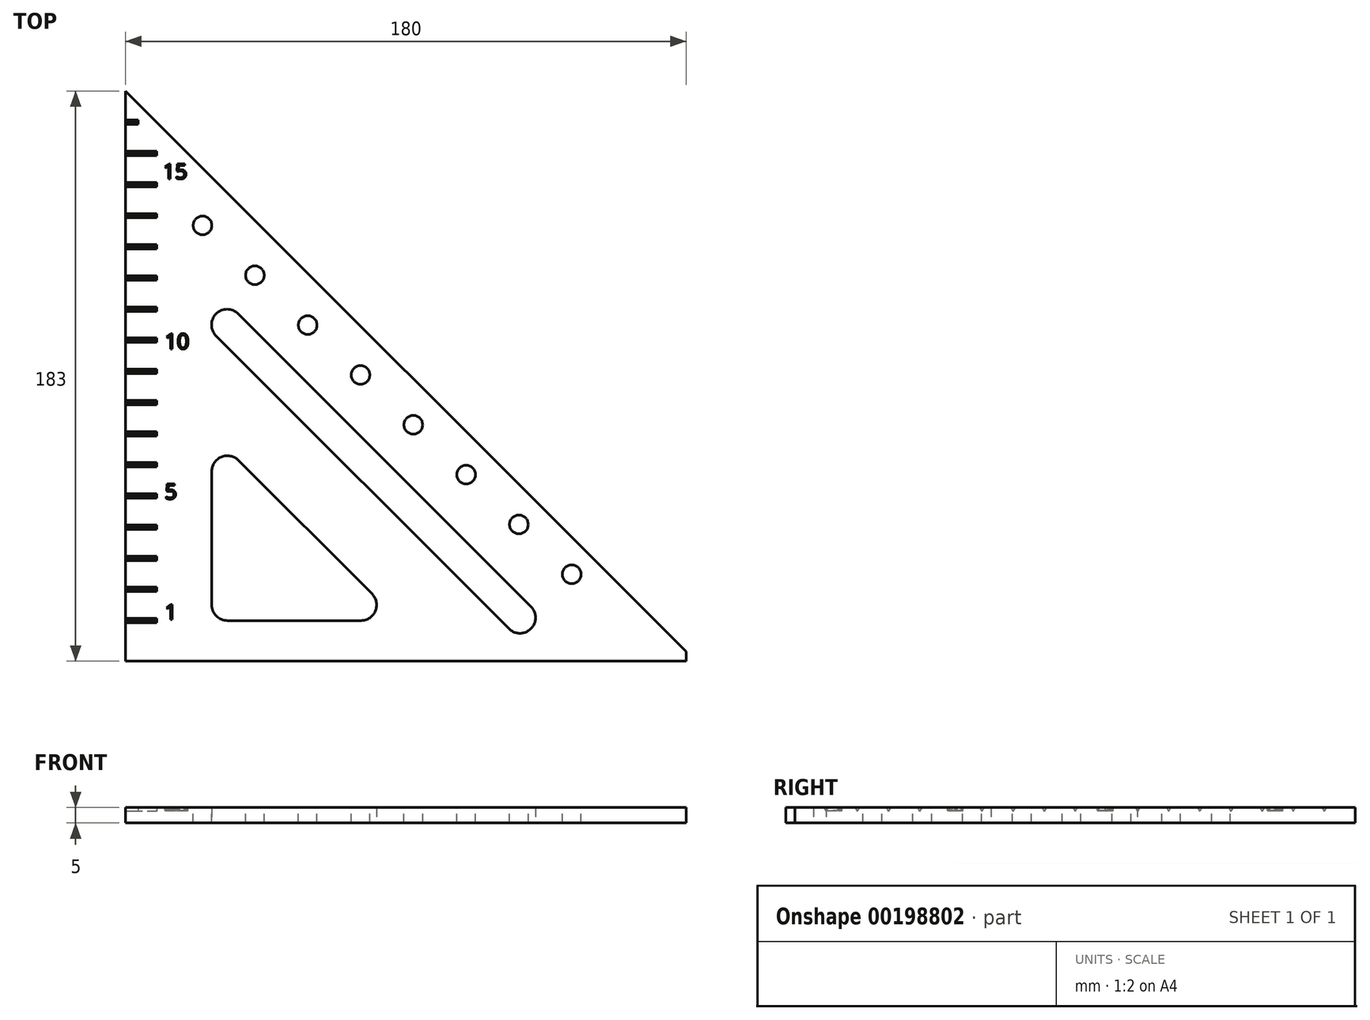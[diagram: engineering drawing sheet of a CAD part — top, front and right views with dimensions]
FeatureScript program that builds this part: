
annotation { "Feature Type Name" : "Feature", "Feature Type Description" : "" }
export const myFeature = defineFeature(function(context is Context, id is Id, definition is map)
    precondition{}
    {
        {
            var Q0;
            Q0=qCreatedBy(makeId("Top.planeOp"),FACE);
            var sketch = newSketch(context, id + "F0", { "sketchPlane" : qUnion([Q0])});
            skLineSegment(sketch, "E0", {"start": v(-55.4, -72.48) * mm, "end": v(124.6, -72.48) * mm});
            skLineSegment(sketch, "E1", {"start": v(124.6, -72.48) * mm, "end": v(-55.4, 107.52) * mm});
            skLineSegment(sketch, "E2", {"start": v(-55.4, 107.52) * mm, "end": v(-55.4, -72.48) * mm});
            skLineSegment(sketch, "E3", {"start": v(-73.6, 83.28) * mm, "end": v(83.51, -73.83) * mm, "construction": true});
            skLineSegment(sketch, "E4", {"start": v(-27.73, -14.56) * mm, "end": v(-27.73, -57.48) * mm});
            skLineSegment(sketch, "E5", {"start": v(-22.73, -62.48) * mm, "end": v(20.2, -62.48) * mm});
            skLineSegment(sketch, "E6", {"start": v(23.74, -53.95) * mm, "end": v(-19.19, -11.02) * mm});
            skPoint(sketch, "E7.visualSharp", {"position": v(-27.73, -62.48) * mm});
            skArc(sketch, "E7.filletArc", {"start": v(-27.73, -57.48) * mm, "mid": v(-26.26, -61.02) * mm, "end": v(-22.73, -62.48) * mm});
            skPoint(sketch, "E8.visualSharp", {"position": v(32.27, -62.48) * mm});
            skArc(sketch, "E8.filletArc", {"start": v(20.2, -62.48) * mm, "mid": v(24.82, -59.4) * mm, "end": v(23.74, -53.95) * mm});
            skPoint(sketch, "E9.visualSharp", {"position": v(-27.73, -2.48) * mm});
            skArc(sketch, "E9.filletArc", {"start": v(-19.19, -11.02) * mm, "mid": v(-24.64, -9.94) * mm, "end": v(-27.73, -14.56) * mm});
            skLineSegment(sketch, "E10", {"start": v(-19.27, 36.02) * mm, "end": v(74.78, -58.03) * mm});
            skLineSegment(sketch, "E11.MirrorCS", {"start": v(-26.34, 28.95) * mm, "end": v(67.7, -65.1) * mm});
            skLineSegment(sketch, "E12", {"start": v(-27.73, -25.02) * mm, "end": v(-27.73, 82.1) * mm, "construction": true});
            skArc(sketch, "E13", {"start": v(-19.27, 36.02) * mm, "mid": v(-26.34, 36.02) * mm, "end": v(-26.34, 28.95) * mm});
            skArc(sketch, "E14", {"start": v(67.7, -65.1) * mm, "mid": v(74.78, -65.1) * mm, "end": v(74.78, -58.03) * mm});
            skLineSegment(sketch, "E15", {"start": v(-55.4, -98.03) * mm, "end": v(-55.4, 125.94) * mm, "construction": true});
            skLineSegment(sketch, "E16", {"start": v(-63.27, -62.48) * mm, "end": v(-48.03, -62.48) * mm, "construction": true});
            skLineSegment(sketch, "E17.bottom", {"start": v(-55.4, -72.48) * mm, "end": v(124.59, -72.48) * mm});
            skLineSegment(sketch, "E17.top", {"start": v(-55.4, -75.48) * mm, "end": v(124.59, -75.48) * mm});
            skLineSegment(sketch, "E17.left", {"start": v(-55.4, -72.48) * mm, "end": v(-55.4, -75.48) * mm});
            skLineSegment(sketch, "E17.right", {"start": v(124.59, -72.48) * mm, "end": v(124.59, -75.48) * mm});
            skLineSegment(sketch, "E18", {"start": v(-62.17, 97.41) * mm, "end": v(117.66, -82.41) * mm, "construction": true});
            skLineSegment(sketch, "E19", {"start": v(-55.4, -72.48) * mm, "end": v(144.22, -19) * mm, "construction": true});
            skLineSegment(sketch, "E20", {"start": v(-55.4, -72.48) * mm, "end": v(114.68, 25.72) * mm, "construction": true});
            skLineSegment(sketch, "E21", {"start": v(-55.4, -72.48) * mm, "end": v(71.5, 54.43) * mm, "construction": true});
            skLineSegment(sketch, "E22", {"start": v(-55.4, -72.48) * mm, "end": v(37.85, 89.04) * mm, "construction": true});
            skLineSegment(sketch, "E23", {"start": v(-55.4, -72.48) * mm, "end": v(-6.43, 110.3) * mm, "construction": true});
            skLineSegment(sketch, "E24", {"start": v(73.26, -38) * mm, "end": v(86.55, -34.45) * mm});
            skLineSegment(sketch, "E25", {"start": v(48.02, -12.77) * mm, "end": v(58.7, -6.6) * mm});
            skLineSegment(sketch, "E26", {"start": v(26.16, 9.09) * mm, "end": v(34.6, 17.52) * mm});
            skLineSegment(sketch, "E27", {"start": v(4.3, 30.94) * mm, "end": v(10.47, 41.63) * mm});
            skLineSegment(sketch, "E28", {"start": v(-20.93, 56.18) * mm, "end": v(-17.37, 69.48) * mm});
            skSolve(sketch);
        }
        {
            var Q0;
            Q0 = qSketchRegion(id + "F0", true);
            extrude(context, id + "F1", {"entities" : qUnion([Q0]), "endBound" : BoundingType.SYMMETRIC, "depth" : 5 * mm});
        }
        {
            var Q0;
            Q0=makeQuery(id+"F1.opExtrude","SWEPT_FACE",FACE,{"disambiguationData":[OSD([sQuery(id+"F0.wireOp",EDGE,"E2"),sQuery(id+"F0.wireOp",EDGE,"E17.left")])]});
            cPlane(context, id + "F2", {"entities" : qUnion([Q0]), "cplaneType" : CPlaneType.OFFSET, "offset" : 0 * mm, "width" : 150 * mm, "height" : 150 * mm});
        }
        {
            var Q0;
            Q0=qCreatedBy(id+"F2.planeOp",FACE);
            var sketch = newSketch(context, id + "F3", { "sketchPlane" : qUnion([Q0])});
            skLineSegment(sketch, "E29", {"start": v(72.48, 5.08) * mm, "end": v(72.48, -6.06) * mm, "construction": true});
            skLineSegment(sketch, "E30", {"start": v(62.48, 3.35) * mm, "end": v(62.48, -6.25) * mm, "construction": true});
            skLineSegment(sketch, "E31", {"start": v(62.48, 2.51) * mm, "end": v(61.78, 2.51) * mm});
            skLineSegment(sketch, "E32", {"start": v(61.78, 2.51) * mm, "end": v(62.48, 1.19) * mm});
            skLineSegment(sketch, "E33.MirrorCS", {"start": v(62.48, -0.72) * mm, "end": v(62.48, 8.88) * mm, "construction": true});
            skLineSegment(sketch, "E34.MirrorCS", {"start": v(62.48, 2.51) * mm, "end": v(63.18, 2.51) * mm});
            skLineSegment(sketch, "E35.MirrorCS", {"start": v(63.18, 2.51) * mm, "end": v(62.48, 1.19) * mm});
            skLineSegment(sketch, "E36.1.0.0", {"start": v(51.78, 2.51) * mm, "end": v(52.48, 1.19) * mm});
            skLineSegment(sketch, "E36.1.0.1", {"start": v(53.18, 2.51) * mm, "end": v(52.48, 1.19) * mm});
            skLineSegment(sketch, "E36.1.0.2", {"start": v(52.48, 2.51) * mm, "end": v(51.78, 2.51) * mm});
            skLineSegment(sketch, "E36.1.0.3", {"start": v(52.48, 2.51) * mm, "end": v(53.18, 2.51) * mm});
            skLineSegment(sketch, "E36.2.0.0", {"start": v(41.78, 2.51) * mm, "end": v(42.48, 1.19) * mm});
            skLineSegment(sketch, "E36.2.0.1", {"start": v(43.18, 2.51) * mm, "end": v(42.48, 1.19) * mm});
            skLineSegment(sketch, "E36.2.0.2", {"start": v(42.48, 2.51) * mm, "end": v(41.78, 2.51) * mm});
            skLineSegment(sketch, "E36.2.0.3", {"start": v(42.48, 2.51) * mm, "end": v(43.18, 2.51) * mm});
            skLineSegment(sketch, "E36.3.0.0", {"start": v(31.78, 2.51) * mm, "end": v(32.48, 1.19) * mm});
            skLineSegment(sketch, "E36.3.0.1", {"start": v(33.18, 2.51) * mm, "end": v(32.48, 1.19) * mm});
            skLineSegment(sketch, "E36.3.0.2", {"start": v(32.48, 2.51) * mm, "end": v(31.78, 2.51) * mm});
            skLineSegment(sketch, "E36.3.0.3", {"start": v(32.48, 2.51) * mm, "end": v(33.18, 2.51) * mm});
            skLineSegment(sketch, "E36.4.0.0", {"start": v(21.78, 2.51) * mm, "end": v(22.48, 1.19) * mm});
            skLineSegment(sketch, "E36.4.0.1", {"start": v(23.18, 2.51) * mm, "end": v(22.48, 1.19) * mm});
            skLineSegment(sketch, "E36.4.0.2", {"start": v(22.48, 2.51) * mm, "end": v(21.78, 2.51) * mm});
            skLineSegment(sketch, "E36.4.0.3", {"start": v(22.48, 2.51) * mm, "end": v(23.18, 2.51) * mm});
            skLineSegment(sketch, "E36.5.0.0", {"start": v(11.78, 2.51) * mm, "end": v(12.48, 1.19) * mm});
            skLineSegment(sketch, "E36.5.0.1", {"start": v(13.18, 2.51) * mm, "end": v(12.48, 1.19) * mm});
            skLineSegment(sketch, "E36.5.0.2", {"start": v(12.48, 2.51) * mm, "end": v(11.78, 2.51) * mm});
            skLineSegment(sketch, "E36.5.0.3", {"start": v(12.48, 2.51) * mm, "end": v(13.18, 2.51) * mm});
            skLineSegment(sketch, "E36.6.0.0", {"start": v(1.78, 2.51) * mm, "end": v(2.48, 1.19) * mm});
            skLineSegment(sketch, "E36.6.0.1", {"start": v(3.18, 2.51) * mm, "end": v(2.48, 1.19) * mm});
            skLineSegment(sketch, "E36.6.0.2", {"start": v(2.48, 2.51) * mm, "end": v(1.78, 2.51) * mm});
            skLineSegment(sketch, "E36.6.0.3", {"start": v(2.48, 2.51) * mm, "end": v(3.18, 2.51) * mm});
            skLineSegment(sketch, "E36.7.0.0", {"start": v(-8.22, 2.51) * mm, "end": v(-7.52, 1.19) * mm});
            skLineSegment(sketch, "E36.7.0.1", {"start": v(-6.82, 2.51) * mm, "end": v(-7.52, 1.19) * mm});
            skLineSegment(sketch, "E36.7.0.2", {"start": v(-7.52, 2.51) * mm, "end": v(-8.22, 2.51) * mm});
            skLineSegment(sketch, "E36.7.0.3", {"start": v(-7.52, 2.51) * mm, "end": v(-6.82, 2.51) * mm});
            skLineSegment(sketch, "E36.8.0.0", {"start": v(-18.22, 2.51) * mm, "end": v(-17.52, 1.19) * mm});
            skLineSegment(sketch, "E36.8.0.1", {"start": v(-16.82, 2.51) * mm, "end": v(-17.52, 1.19) * mm});
            skLineSegment(sketch, "E36.8.0.2", {"start": v(-17.52, 2.51) * mm, "end": v(-18.22, 2.51) * mm});
            skLineSegment(sketch, "E36.8.0.3", {"start": v(-17.52, 2.51) * mm, "end": v(-16.82, 2.51) * mm});
            skLineSegment(sketch, "E36.9.0.0", {"start": v(-28.22, 2.51) * mm, "end": v(-27.52, 1.19) * mm});
            skLineSegment(sketch, "E36.9.0.1", {"start": v(-26.82, 2.51) * mm, "end": v(-27.52, 1.19) * mm});
            skLineSegment(sketch, "E36.9.0.2", {"start": v(-27.52, 2.51) * mm, "end": v(-28.22, 2.51) * mm});
            skLineSegment(sketch, "E36.9.0.3", {"start": v(-27.52, 2.51) * mm, "end": v(-26.82, 2.51) * mm});
            skLineSegment(sketch, "E36.10.0.0", {"start": v(-38.22, 2.51) * mm, "end": v(-37.52, 1.19) * mm});
            skLineSegment(sketch, "E36.10.0.1", {"start": v(-36.82, 2.51) * mm, "end": v(-37.52, 1.19) * mm});
            skLineSegment(sketch, "E36.10.0.2", {"start": v(-37.52, 2.51) * mm, "end": v(-38.22, 2.51) * mm});
            skLineSegment(sketch, "E36.10.0.3", {"start": v(-37.52, 2.51) * mm, "end": v(-36.82, 2.51) * mm});
            skLineSegment(sketch, "E36.11.0.0", {"start": v(-48.22, 2.51) * mm, "end": v(-47.52, 1.19) * mm});
            skLineSegment(sketch, "E36.11.0.1", {"start": v(-46.82, 2.51) * mm, "end": v(-47.52, 1.19) * mm});
            skLineSegment(sketch, "E36.11.0.2", {"start": v(-47.52, 2.51) * mm, "end": v(-48.22, 2.51) * mm});
            skLineSegment(sketch, "E36.11.0.3", {"start": v(-47.52, 2.51) * mm, "end": v(-46.82, 2.51) * mm});
            skLineSegment(sketch, "E36.12.0.0", {"start": v(-58.22, 2.51) * mm, "end": v(-57.52, 1.19) * mm});
            skLineSegment(sketch, "E36.12.0.1", {"start": v(-56.82, 2.51) * mm, "end": v(-57.52, 1.19) * mm});
            skLineSegment(sketch, "E36.12.0.2", {"start": v(-57.52, 2.51) * mm, "end": v(-58.22, 2.51) * mm});
            skLineSegment(sketch, "E36.12.0.3", {"start": v(-57.52, 2.51) * mm, "end": v(-56.82, 2.51) * mm});
            skLineSegment(sketch, "E36.13.0.0", {"start": v(-68.22, 2.51) * mm, "end": v(-67.52, 1.19) * mm});
            skLineSegment(sketch, "E36.13.0.1", {"start": v(-66.82, 2.51) * mm, "end": v(-67.52, 1.19) * mm});
            skLineSegment(sketch, "E36.13.0.2", {"start": v(-67.52, 2.51) * mm, "end": v(-68.22, 2.51) * mm});
            skLineSegment(sketch, "E36.13.0.3", {"start": v(-67.52, 2.51) * mm, "end": v(-66.82, 2.51) * mm});
            skLineSegment(sketch, "E36.14.0.0", {"start": v(-78.22, 2.51) * mm, "end": v(-77.52, 1.19) * mm});
            skLineSegment(sketch, "E36.14.0.1", {"start": v(-76.82, 2.51) * mm, "end": v(-77.52, 1.19) * mm});
            skLineSegment(sketch, "E36.14.0.2", {"start": v(-77.52, 2.51) * mm, "end": v(-78.22, 2.51) * mm});
            skLineSegment(sketch, "E36.14.0.3", {"start": v(-77.52, 2.51) * mm, "end": v(-76.82, 2.51) * mm});
            skLineSegment(sketch, "E36.15.0.0", {"start": v(-88.22, 2.51) * mm, "end": v(-87.52, 1.19) * mm});
            skLineSegment(sketch, "E36.15.0.1", {"start": v(-86.82, 2.51) * mm, "end": v(-87.52, 1.19) * mm});
            skLineSegment(sketch, "E36.15.0.2", {"start": v(-87.52, 2.51) * mm, "end": v(-88.22, 2.51) * mm});
            skLineSegment(sketch, "E36.15.0.3", {"start": v(-87.52, 2.51) * mm, "end": v(-86.82, 2.51) * mm});
            skLineSegment(sketch, "E36.16.0.0", {"start": v(-98.22, 2.51) * mm, "end": v(-97.52, 1.19) * mm});
            skLineSegment(sketch, "E36.16.0.1", {"start": v(-96.82, 2.51) * mm, "end": v(-97.52, 1.19) * mm});
            skLineSegment(sketch, "E36.16.0.2", {"start": v(-97.52, 2.51) * mm, "end": v(-98.22, 2.51) * mm});
            skLineSegment(sketch, "E36.16.0.3", {"start": v(-97.52, 2.51) * mm, "end": v(-96.82, 2.51) * mm});
            skLineSegment(sketch, "E36.direction1", {"start": v(62.48, -0.01) * mm, "end": v(52.48, -0.01) * mm, "construction": true});
            skSolve(sketch);
        }
        {
            var Q0;
            Q0=makeQuery(id+"F3.imprint","IMPRINT",FACE,{"disambiguationData":[TD([[makeQuery(id+"F3.imprint","IMPRINT",EDGE,{"derivedFrom":sQuery(id+"F3.wireOp",EDGE,"E31")}),1.0]])]});
            var Q1;
            Q1=makeQuery(id+"F3.imprint","IMPRINT",FACE,{"disambiguationData":[TD([[makeQuery(id+"F3.imprint","IMPRINT",EDGE,{"derivedFrom":sQuery(id+"F3.wireOp",EDGE,"E36.1.0.0")}),1.0]])]});
            var Q2;
            Q2=makeQuery(id+"F3.imprint","IMPRINT",FACE,{"disambiguationData":[TD([[makeQuery(id+"F3.imprint","IMPRINT",EDGE,{"derivedFrom":sQuery(id+"F3.wireOp",EDGE,"E36.2.0.0")}),1.0]])]});
            var Q3;
            Q3=makeQuery(id+"F3.imprint","IMPRINT",FACE,{"disambiguationData":[TD([[makeQuery(id+"F3.imprint","IMPRINT",EDGE,{"derivedFrom":sQuery(id+"F3.wireOp",EDGE,"E36.3.0.0")}),1.0]])]});
            var Q4;
            Q4=makeQuery(id+"F3.imprint","IMPRINT",FACE,{"disambiguationData":[TD([[makeQuery(id+"F3.imprint","IMPRINT",EDGE,{"derivedFrom":sQuery(id+"F3.wireOp",EDGE,"E36.4.0.0")}),1.0]])]});
            var Q5;
            Q5=makeQuery(id+"F3.imprint","IMPRINT",FACE,{"disambiguationData":[TD([[makeQuery(id+"F3.imprint","IMPRINT",EDGE,{"derivedFrom":sQuery(id+"F3.wireOp",EDGE,"E36.5.0.0")}),1.0]])]});
            var Q6;
            Q6=makeQuery(id+"F3.imprint","IMPRINT",FACE,{"disambiguationData":[TD([[makeQuery(id+"F3.imprint","IMPRINT",EDGE,{"derivedFrom":sQuery(id+"F3.wireOp",EDGE,"E36.6.0.0")}),1.0]])]});
            var Q7;
            Q7=makeQuery(id+"F3.imprint","IMPRINT",FACE,{"disambiguationData":[TD([[makeQuery(id+"F3.imprint","IMPRINT",EDGE,{"derivedFrom":sQuery(id+"F3.wireOp",EDGE,"E36.7.0.0")}),1.0]])]});
            var Q8;
            Q8=makeQuery(id+"F3.imprint","IMPRINT",FACE,{"disambiguationData":[TD([[makeQuery(id+"F3.imprint","IMPRINT",EDGE,{"derivedFrom":sQuery(id+"F3.wireOp",EDGE,"E36.8.0.0")}),1.0]])]});
            var Q9;
            Q9=makeQuery(id+"F3.imprint","IMPRINT",FACE,{"disambiguationData":[TD([[makeQuery(id+"F3.imprint","IMPRINT",EDGE,{"derivedFrom":sQuery(id+"F3.wireOp",EDGE,"E36.9.0.0")}),1.0]])]});
            var Q10;
            Q10=makeQuery(id+"F3.imprint","IMPRINT",FACE,{"disambiguationData":[TD([[makeQuery(id+"F3.imprint","IMPRINT",EDGE,{"derivedFrom":sQuery(id+"F3.wireOp",EDGE,"E36.10.0.0")}),1.0]])]});
            var Q11;
            Q11=makeQuery(id+"F3.imprint","IMPRINT",FACE,{"disambiguationData":[TD([[makeQuery(id+"F3.imprint","IMPRINT",EDGE,{"derivedFrom":sQuery(id+"F3.wireOp",EDGE,"E36.11.0.0")}),1.0]])]});
            var Q12;
            Q12=makeQuery(id+"F3.imprint","IMPRINT",FACE,{"disambiguationData":[TD([[makeQuery(id+"F3.imprint","IMPRINT",EDGE,{"derivedFrom":sQuery(id+"F3.wireOp",EDGE,"E36.12.0.0")}),1.0]])]});
            var Q13;
            Q13=makeQuery(id+"F3.imprint","IMPRINT",FACE,{"disambiguationData":[TD([[makeQuery(id+"F3.imprint","IMPRINT",EDGE,{"derivedFrom":sQuery(id+"F3.wireOp",EDGE,"E36.13.0.0")}),1.0]])]});
            var Q14;
            Q14=makeQuery(id+"F3.imprint","IMPRINT",FACE,{"disambiguationData":[TD([[makeQuery(id+"F3.imprint","IMPRINT",EDGE,{"derivedFrom":sQuery(id+"F3.wireOp",EDGE,"E36.14.0.0")}),1.0]])]});
            var Q15;
            Q15=makeQuery(id+"F3.imprint","IMPRINT",FACE,{"disambiguationData":[TD([[makeQuery(id+"F3.imprint","IMPRINT",EDGE,{"derivedFrom":sQuery(id+"F3.wireOp",EDGE,"E36.15.0.0")}),1.0]])]});
            extrude(context, id + "F4", {"entities" : qUnion([Q0, Q1, Q2, Q3, Q4, Q5, Q6, Q7, Q8, Q9, Q10, Q11, Q12, Q13, Q14, Q15]), "operationType" : NewBodyOperationType.REMOVE, "oppositeDirection" : true, "depth" : 10 * mm});
        }
        {
            var Q0;
            Q0=makeQuery(id+"F3.imprint","IMPRINT",FACE,{"disambiguationData":[TD([[makeQuery(id+"F3.imprint","IMPRINT",EDGE,{"derivedFrom":sQuery(id+"F3.wireOp",EDGE,"E36.16.0.0")}),1.0]])]});
            extrude(context, id + "F5", {"entities" : qUnion([Q0]), "operationType" : NewBodyOperationType.REMOVE, "oppositeDirection" : true, "depth" : 4 * mm});
        }
        {
            var Q0;
            Q0=makeQuery(id+"F1.opExtrude","CAP_FACE",FACE,{"disambiguationData":[OSD([sQuery(id+"F0.wireOp",EDGE,"E0"),sQuery(id+"F0.wireOp",EDGE,"E1"),sQuery(id+"F0.wireOp",EDGE,"E2"),sQuery(id+"F0.wireOp",EDGE,"E4"),sQuery(id+"F0.wireOp",EDGE,"E5"),sQuery(id+"F0.wireOp",EDGE,"E6"),sQuery(id+"F0.wireOp",EDGE,"E7.filletArc"),sQuery(id+"F0.wireOp",EDGE,"E8.filletArc"),sQuery(id+"F0.wireOp",EDGE,"E9.filletArc"),sQuery(id+"F0.wireOp",EDGE,"E10"),sQuery(id+"F0.wireOp",EDGE,"E11.MirrorCS"),sQuery(id+"F0.wireOp",EDGE,"E13"),sQuery(id+"F0.wireOp",EDGE,"E14"),sQuery(id+"F0.wireOp",EDGE,"E17.top"),sQuery(id+"F0.wireOp",EDGE,"E17.left"),sQuery(id+"F0.wireOp",EDGE,"E17.right")])],"isStart":false});
            cPlane(context, id + "F6", {"entities" : qUnion([Q0]), "cplaneType" : CPlaneType.OFFSET, "offset" : 0 * mm, "width" : 150 * mm, "height" : 150 * mm});
        }
        {
            var Q0;
            Q0=qCreatedBy(id+"F6.planeOp",FACE);
            var sketch = newSketch(context, id + "F7", { "sketchPlane" : qUnion([Q0])});
            skLineSegment(sketch, "E37", {"start": v(-43.4, -65.1) * mm, "end": v(-43.4, 109.4) * mm, "construction": true});
            skCircle(sketch, "E38", {"center": v(-30.7, 64.38) * mm, "radius": 3 * mm});
            skLineSegment(sketch, "E39", {"start": v(-60.24, 92.11) * mm, "end": v(118.2, -76.23) * mm, "construction": true});
            skText(sketch, "E40", { "text": "1", "fontName": "OpenSans-Regular.ttf"});
            skText(sketch, "E41", { "text": "10", "fontName": "OpenSans-Regular.ttf"});
            skText(sketch, "E42", { "text": "5", "fontName": "OpenSans-Regular.ttf"});
            skText(sketch, "E43", { "text": "15\n", "fontName": "OpenSans-Regular.ttf"});
            skCircle(sketch, "E44", {"center": v(-13.89, 48.38) * mm, "radius": 3 * mm});
            skCircle(sketch, "E45", {"center": v(3.07, 32.38) * mm, "radius": 3 * mm});
            skCircle(sketch, "E46", {"center": v(20.03, 16.38) * mm, "radius": 3 * mm});
            skCircle(sketch, "E47", {"center": v(37, 0.38) * mm, "radius": 3 * mm});
            skCircle(sketch, "E48", {"center": v(53.96, -15.62) * mm, "radius": 3 * mm});
            skCircle(sketch, "E49", {"center": v(70.92, -31.62) * mm, "radius": 3 * mm});
            skCircle(sketch, "E50", {"center": v(87.88, -47.62) * mm, "radius": 3 * mm});
            const initialGuessF7  = {"E40": [-0.04282, -0.06221, 1, 0, 0.00491], "E41": [-0.04281, 0.02474, 1, 0, 0.00491], "E42": [-0.04283, -0.02345, 1, 0, 0.00491], "E43": [-0.04341, 0.07933, 1, 0, 0.00491]};
            skSetInitialGuess(sketch, initialGuessF7);
            skSolve(sketch);
        }
        {
            var Q0;
            Q0=makeQuery(id+"F7.imprint","IMPRINT",FACE,{"disambiguationData":[TD([[makeQuery(id+"F7.imprint","IMPRINT",EDGE,{"derivedFrom":sQuery(id+"F7.wireOp",EDGE,"E38")}),1.0]])]});
            extrude(context, id + "F8", {"entities" : qUnion([Q0]), "operationType" : NewBodyOperationType.REMOVE, "oppositeDirection" : true, "depth" : 10 * mm});
        }
        {
            var Q0;
            Q0 = qSketchRegion(id + "F7", true);
            extrude(context, id + "F9", {"entities" : qUnion([Q0]), "operationType" : NewBodyOperationType.REMOVE, "oppositeDirection" : true, "depth" : 1 * mm});
        }
        {
            var Q0;
            Q0=makeQuery(id+"F7.imprint","IMPRINT",FACE,{"disambiguationData":[TD([[makeQuery(id+"F7.imprint","IMPRINT",EDGE,{"derivedFrom":sQuery(id+"F7.wireOp",EDGE,"E38")}),1.0]])]});
            var Q1;
            Q1=sQuery(id+"F7.wireOp",EDGE,"E38");
            extrude(context, id + "F10", {"entities" : qUnion([Q0]), "operationType" : NewBodyOperationType.REMOVE, "surfaceEntities" : qUnion([Q1]), "endBound" : BoundingType.SYMMETRIC, "oppositeDirection" : true, "depth" : 25 * mm});
        }
        {
            var Q0;
            Q0=makeQuery(id+"F7.imprint","IMPRINT",FACE,{"disambiguationData":[TD([[makeQuery(id+"F7.imprint","IMPRINT",EDGE,{"derivedFrom":sQuery(id+"F7.wireOp",EDGE,"E38")}),1.0]])]});
            var Q1;
            Q1=makeQuery(id+"F7.imprint","IMPRINT",FACE,{"disambiguationData":[TD([[makeQuery(id+"F7.imprint","IMPRINT",EDGE,{"derivedFrom":sQuery(id+"F7.wireOp",EDGE,"E44")}),1.0]])]});
            var Q2;
            Q2=makeQuery(id+"F7.imprint","IMPRINT",FACE,{"disambiguationData":[TD([[makeQuery(id+"F7.imprint","IMPRINT",EDGE,{"derivedFrom":sQuery(id+"F7.wireOp",EDGE,"E45")}),1.0]])]});
            var Q3;
            Q3=makeQuery(id+"F7.imprint","IMPRINT",FACE,{"disambiguationData":[TD([[makeQuery(id+"F7.imprint","IMPRINT",EDGE,{"derivedFrom":sQuery(id+"F7.wireOp",EDGE,"E46")}),1.0]])]});
            var Q4;
            Q4=makeQuery(id+"F7.imprint","IMPRINT",FACE,{"disambiguationData":[TD([[makeQuery(id+"F7.imprint","IMPRINT",EDGE,{"derivedFrom":sQuery(id+"F7.wireOp",EDGE,"E47")}),1.0]])]});
            var Q5;
            Q5=makeQuery(id+"F7.imprint","IMPRINT",FACE,{"disambiguationData":[TD([[makeQuery(id+"F7.imprint","IMPRINT",EDGE,{"derivedFrom":sQuery(id+"F7.wireOp",EDGE,"E48")}),1.0]])]});
            var Q6;
            Q6=makeQuery(id+"F7.imprint","IMPRINT",FACE,{"disambiguationData":[TD([[makeQuery(id+"F7.imprint","IMPRINT",EDGE,{"derivedFrom":sQuery(id+"F7.wireOp",EDGE,"E49")}),1.0]])]});
            var Q7;
            Q7=makeQuery(id+"F7.imprint","IMPRINT",FACE,{"disambiguationData":[TD([[makeQuery(id+"F7.imprint","IMPRINT",EDGE,{"derivedFrom":sQuery(id+"F7.wireOp",EDGE,"E50")}),1.0]])]});
            extrude(context, id + "F11", {"entities" : qUnion([Q0, Q1, Q2, Q3, Q4, Q5, Q6, Q7]), "operationType" : NewBodyOperationType.REMOVE, "endBound" : BoundingType.THROUGH_ALL, "oppositeDirection" : true, "depth" : 25 * mm});
        }
    });
